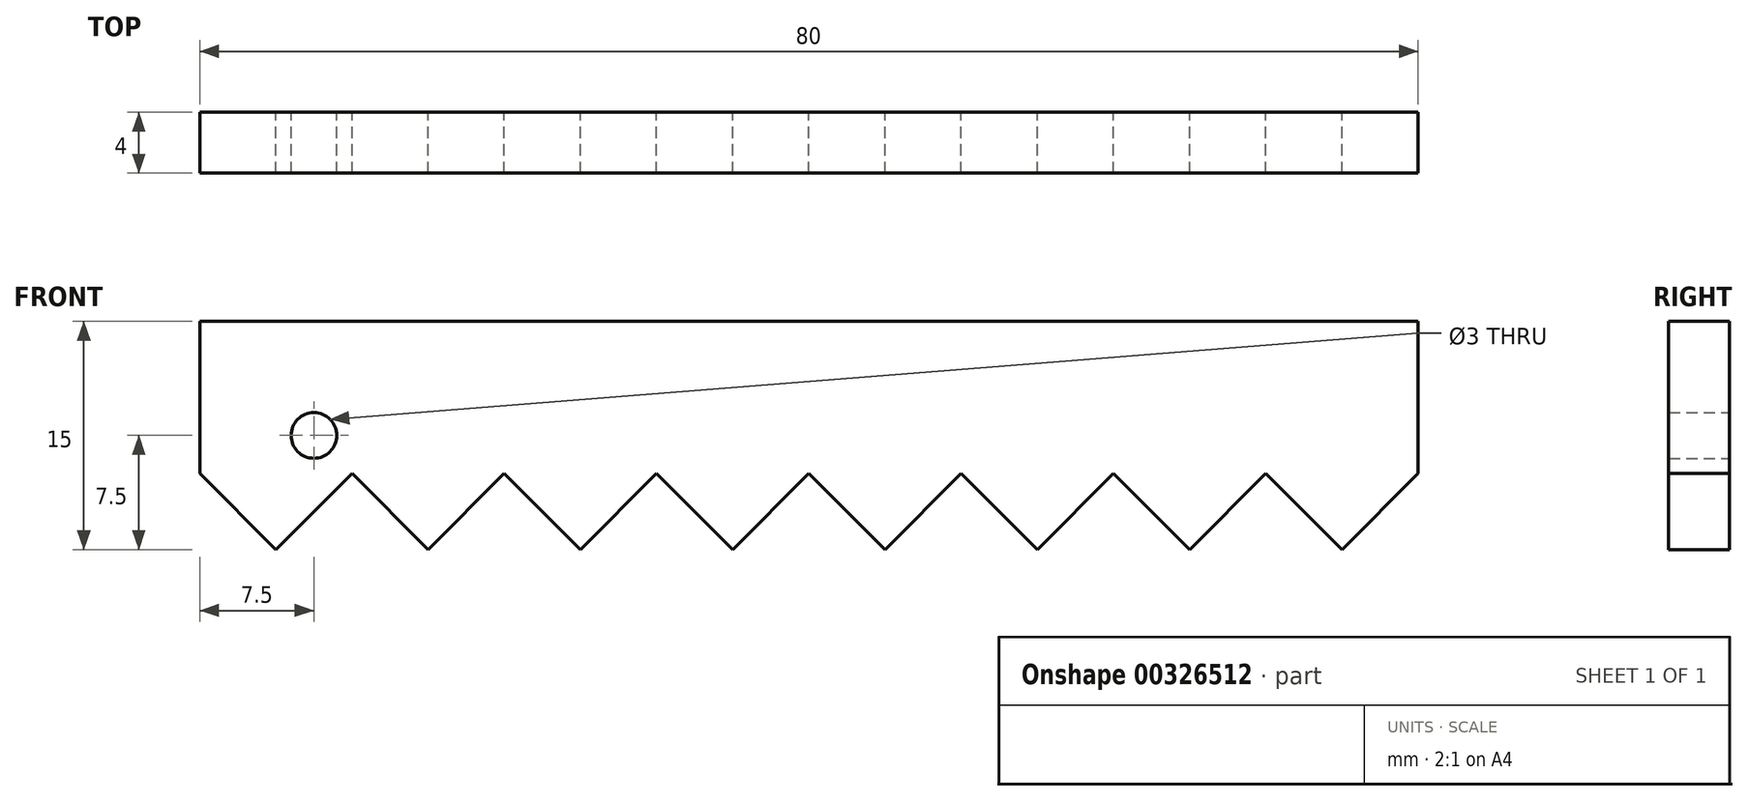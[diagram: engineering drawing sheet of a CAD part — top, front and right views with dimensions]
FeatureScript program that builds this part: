
annotation { "Feature Type Name" : "Feature", "Feature Type Description" : "" }
export const myFeature = defineFeature(function(context is Context, id is Id, definition is map)
    precondition{}
    {
        {
            var Q0;
            Q0=qCreatedBy(makeId("Front.planeOp"),FACE);
            var sketch = newSketch(context, id + "F0", { "sketchPlane" : qUnion([Q0])});
            skLineSegment(sketch, "E0.top", {"start": v(0, 15) * mm, "end": v(80, 15) * mm});
            skLineSegment(sketch, "E0.left", {"start": v(0, 5) * mm, "end": v(0, 15) * mm});
            skLineSegment(sketch, "E0.right", {"start": v(80, 5) * mm, "end": v(80, 15) * mm});
            skLineSegment(sketch, "E1", {"start": v(0, 7.5) * mm, "end": v(7.5, 7.5) * mm, "construction": true});
            skCircle(sketch, "E2", {"center": v(7.5, 7.5) * mm, "radius": 1.5 * mm});
            skLineSegment(sketch, "E3", {"start": v(0, 5) * mm, "end": v(10, 5) * mm, "construction": true});
            skLineSegment(sketch, "E4", {"start": v(10, 5) * mm, "end": v(20, 5) * mm, "construction": true});
            skLineSegment(sketch, "E5", {"start": v(20, 5) * mm, "end": v(30, 5) * mm, "construction": true});
            skLineSegment(sketch, "E6", {"start": v(30, 5) * mm, "end": v(40, 5) * mm, "construction": true});
            skLineSegment(sketch, "E7", {"start": v(40, 5) * mm, "end": v(50, 5) * mm, "construction": true});
            skLineSegment(sketch, "E8", {"start": v(50, 5) * mm, "end": v(60, 5) * mm, "construction": true});
            skLineSegment(sketch, "E9", {"start": v(60, 5) * mm, "end": v(70, 5) * mm, "construction": true});
            skLineSegment(sketch, "E10", {"start": v(70, 5) * mm, "end": v(80, 5) * mm, "construction": true});
            skLineSegment(sketch, "E11", {"start": v(0, 5) * mm, "end": v(5, 0) * mm});
            skLineSegment(sketch, "E12", {"start": v(5, 0) * mm, "end": v(10, 5) * mm});
            skLineSegment(sketch, "E13", {"start": v(10, 5) * mm, "end": v(15, 0) * mm});
            skLineSegment(sketch, "E14", {"start": v(15, 0) * mm, "end": v(20, 5) * mm});
            skLineSegment(sketch, "E15", {"start": v(20, 5) * mm, "end": v(25, 0) * mm});
            skLineSegment(sketch, "E16", {"start": v(25, 0) * mm, "end": v(30, 5) * mm});
            skLineSegment(sketch, "E17", {"start": v(30, 5) * mm, "end": v(35, 0) * mm});
            skLineSegment(sketch, "E18", {"start": v(35, 0) * mm, "end": v(40, 5) * mm});
            skLineSegment(sketch, "E19", {"start": v(40, 5) * mm, "end": v(45, 0) * mm});
            skLineSegment(sketch, "E20", {"start": v(45, 0) * mm, "end": v(50, 5) * mm});
            skLineSegment(sketch, "E21", {"start": v(50, 5) * mm, "end": v(55, 0) * mm});
            skLineSegment(sketch, "E22", {"start": v(55, 0) * mm, "end": v(60, 5) * mm});
            skLineSegment(sketch, "E23", {"start": v(60, 5) * mm, "end": v(65, 0) * mm});
            skLineSegment(sketch, "E24", {"start": v(65, 0) * mm, "end": v(70, 5) * mm});
            skLineSegment(sketch, "E25", {"start": v(70, 5) * mm, "end": v(75, 0) * mm});
            skLineSegment(sketch, "E26", {"start": v(75, 0) * mm, "end": v(80, 5) * mm});
            skPoint(sketch, "E27.orphan", {"position": v(0, 0) * mm});
            skSolve(sketch);
        }
        {
            var Q0;
            Q0=makeQuery(id+"F0.imprint","IMPRINT",FACE,{"disambiguationData":[TD([[makeQuery(id+"F0.imprint","IMPRINT",EDGE,{"derivedFrom":sQuery(id+"F0.wireOp",EDGE,"E0.top")}),-1.0]])]});
            extrude(context, id + "F1", {"entities" : qUnion([Q0]), "depth" : 4 * mm});
        }
    });
